# Revit family: Faucet-Handle-KOHLER-Components-K-77980_1
name_source: partatom
category: Plumbing Fixtures
revit_build: Autodesk Revit 2015 (Build: 20140606_1530(x64)
units: mm (PartAtom-declared; Revit-internal decimal feet)

## types (4) — shared parameters
ADA Compliant = No
Assembly Code = D2010
CW Connection = Yes
Cold Water Inlet = Cold Water Inlet
Date Modified = 04/23/2019
Default Elevation = 32"
Drain Included = No
Faucet Hole Spacing = 4"
Flow Rate = 0 GPM
HW Connection = Yes
Height = 2 3/8"
Hot Water Inlet = Hot Water Inlet
Length = 9 5/8"
Manufacturer = KOHLER Co.
MasterFormat 1995 = 15410
MasterFormat 2004 = 22.41.39
Material = Premium Metal Construction
Pressure = 0.00 psi
Product Documentation Link = https://www.us.kohler.com
Product Name = Components
Product Page URL = http://www.us.kohler.com
Spout Reach = 9 5/8"
URL = https://www.us.kohler.com
Vent Connection = No
Waste Connection = No
Waste Water Outlet = Waste Water Outlet
WaterSense Certified = No
Width = 4"

## per-type parameters (varying)
| type | Description | Finish | Handle Clearance | Handle Height | Lever Handle | Model | Pin Handle | Type |
| Pin Handle,BN-Vibrant Brushed Nickel | Wall-Mount Bathroom Sink Pin Handle | Kohler-Metal-BN-Vibrant_Brushed_Nickel | 3 5/8" | 1 15/32" | No | K-77890-4A-BN | Yes | 2 |
| Pin Handle,CP-Polished Chrome | Wall-Mount Bathroom Sink Pin Handle | Kohler-Metal-CP-Polished_Chrome | 3 5/8" | 1 15/32" | No | K-77890-4A-CP | Yes | 1 |
| Lever Handle,BN-Vibrant Brushed Nickel | Wall-Mount Bathroom Sink Lever Handle | Kohler-Metal-BN-Vibrant_Brushed_Nickel | 2 13/16" | 2 5/32" | Yes | K-77890-4-BN | No | 4 |
| Lever Handle,CP-Polished Chrome | Wall-Mount Bathroom Sink Lever Handle | Kohler-Metal-CP-Polished_Chrome | 2 13/16" | 2 5/32" | Yes | K-77890-4-CP | No | 3 |

## geometry (parser evidence)
native form markers: Sweep x6
no freeform markers — native parametric forms only
